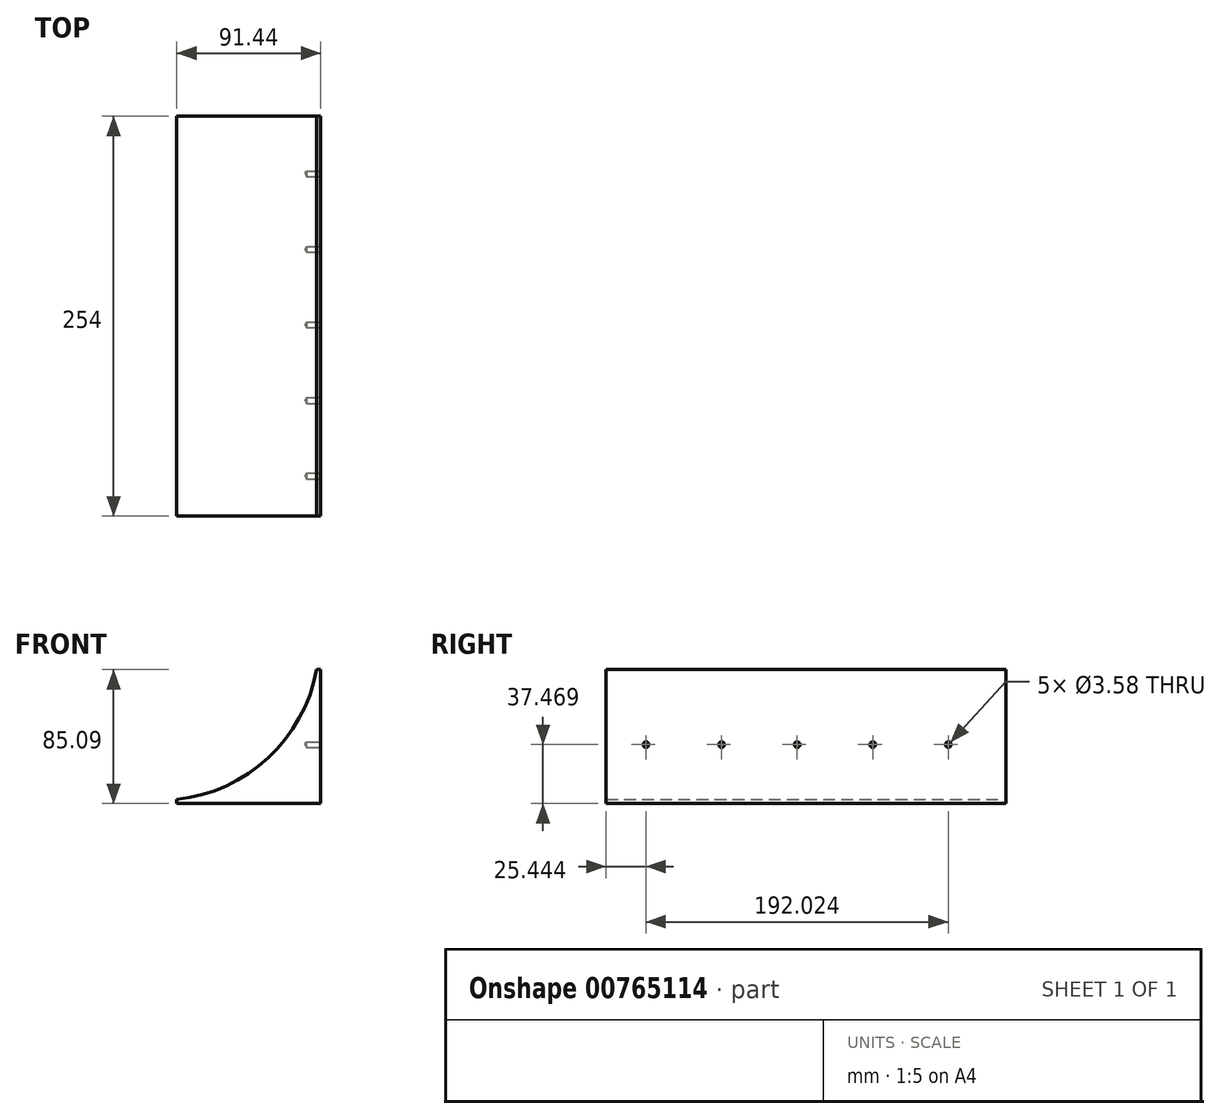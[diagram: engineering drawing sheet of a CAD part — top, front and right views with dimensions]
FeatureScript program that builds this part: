
annotation { "Feature Type Name" : "Feature", "Feature Type Description" : "" }
export const myFeature = defineFeature(function(context is Context, id is Id, definition is map)
    precondition{}
    {
        {
            var Q0;
            Q0=qCreatedBy(makeId("Front.planeOp"),FACE);
            var sketch = newSketch(context, id + "F0", { "sketchPlane" : qUnion([Q0])});
            skLineSegment(sketch, "E0.top", {"start": v(-39.78, -57.04) * mm, "end": v(48.44, -57.04) * mm});
            skLineSegment(sketch, "E1.bottom", {"start": v(49.12, 25.51) * mm, "end": v(61.82, 25.51) * mm});
            skLineSegment(sketch, "E1.top", {"start": v(49.12, -57.04) * mm, "end": v(61.82, -57.04) * mm});
            skLineSegment(sketch, "E1.left", {"start": v(61.82, 25.51) * mm, "end": v(61.82, -57.04) * mm});
            skLineSegment(sketch, "E1.right", {"start": v(49.12, 25.51) * mm, "end": v(49.12, -57.04) * mm});
            skLineSegment(sketch, "E2.bottom", {"start": v(-39.78, -57.04) * mm, "end": v(52.12, -56.76) * mm});
            skLineSegment(sketch, "E3.bottom", {"start": v(-39.78, -57.04) * mm, "end": v(55.47, -57.04) * mm});
            skArc(sketch, "E4", {"start": v(-39.78, -57.04) * mm, "mid": v(18.35, -30.49) * mm, "end": v(49.12, 25.51) * mm});
            skLineSegment(sketch, "E5.bottom", {"start": v(-39.78, -57.04) * mm, "end": v(61.82, -57.04) * mm});
            skLineSegment(sketch, "E5.top", {"start": v(-39.78, -69.74) * mm, "end": v(61.82, -69.74) * mm});
            skLineSegment(sketch, "E5.left", {"start": v(-39.78, -57.04) * mm, "end": v(-39.78, -69.74) * mm});
            skLineSegment(sketch, "E5.right", {"start": v(61.82, -57.04) * mm, "end": v(61.82, -69.74) * mm});
            skSolve(sketch);
        }
        {
            var Q0;
            Q0=qSketchRegion(id+"F0",true);
            extrude(context, id + "F1", {"entities" : qUnion([Q0]), "depth" : 254 * mm, "offsetDistance" : 25.4 * mm});
        }
        {
            var Q0;
            Q0=makeQuery(id+"F1.opExtrude","SWEPT_FACE",FACE,{"disambiguationData":[OSD([sQuery(id+"F0.wireOp",EDGE,"E1.left"),sQuery(id+"F0.wireOp",EDGE,"E5.right")])]});
            var sketch = newSketch(context, id + "F2", { "sketchPlane" : qUnion([Q0])});
            skCircle(sketch, "E6", {"center": v(-228.56, -22.11) * mm, "radius": 1.78 * mm});
            skPoint(sketch, "E6.centerSnap0", {"position": v(-254, -22.11) * mm});
            skCircle(sketch, "E7.1.0.0", {"center": v(-180.55, -22.11) * mm, "radius": 1.78 * mm});
            skCircle(sketch, "E7.2.0.0", {"center": v(-132.54, -22.11) * mm, "radius": 1.78 * mm});
            skCircle(sketch, "E7.3.0.0", {"center": v(-84.54, -22.11) * mm, "radius": 1.78 * mm});
            skCircle(sketch, "E7.4.0.0", {"center": v(-36.53, -22.11) * mm, "radius": 1.78 * mm});
            skLineSegment(sketch, "E7.direction1", {"start": v(-228.56, -22.11) * mm, "end": v(-180.55, -22.11) * mm, "construction": true});
            skSolve(sketch);
        }
        {
            var Q0;
            Q0=sQuery(id+"F2.wireOp",VERTEX,"E6.center");
            var Q1;
            Q1=sQuery(id+"F2.wireOp",VERTEX,"E7.1.0.0.center");
            var Q2;
            Q2=sQuery(id+"F2.wireOp",VERTEX,"E7.2.0.0.center");
            var Q3;
            Q3=sQuery(id+"F2.wireOp",VERTEX,"E7.3.0.0.center");
            var Q4;
            Q4=sQuery(id+"F2.wireOp",VERTEX,"E7.4.0.0.center");
            var Q5;
            Q5=makeQuery(id+"F1.opExtrude","SWEPT_BODY",BODY,{"disambiguationData":[OSD([sQuery(id+"F0.wireOp",EDGE,"E1.bottom"),sQuery(id+"F0.wireOp",EDGE,"E1.left"),sQuery(id+"F0.wireOp",EDGE,"E4"),sQuery(id+"F0.wireOp",EDGE,"E5.top"),sQuery(id+"F0.wireOp",EDGE,"E5.left"),sQuery(id+"F0.wireOp",EDGE,"E5.right")])]});
            hole(context, id + "F3", {"style" : HoleStyle.SIMPLE, "endStyle" : HoleEndStyle.BLIND, "holeDiameter" : 3.58 * mm, "holeDepth" : 19.05 * mm, "isTappedThrough" : true, "tappedDepth" : 12.7 * mm, "tapClearance" : 3, "locations" : qUnion([Q0, Q1, Q2, Q3, Q4]), "scope" : qUnion([Q5])});
        }
        {
            var Q0;
            Q0=makeQuery(id+"F1.opExtrude","SWEPT_FACE",FACE,{"disambiguationData":[OSD([sQuery(id+"F0.wireOp",EDGE,"E1.left"),sQuery(id+"F0.wireOp",EDGE,"E5.right")])]});
            var Q1;
            Q1=makeQuery(id+"F1.opExtrude","CAP_VERTEX",VERTEX,{"disambiguationData":[OSD([sQuery(id+"F0.wireOp",EDGE,"E1.bottom"),sQuery(id+"F0.wireOp",EDGE,"E1.right"),sQuery(id+"F0.wireOp",EDGE,"E4")])],"isStart":false});
            extrude(context, id + "F4", {"entities" : qUnion([Q0]), "operationType" : NewBodyOperationType.REMOVE, "oppositeDirection" : true, "depth" : 10.16 * mm, "endBoundEntityVertex" : qUnion([Q1]), "offsetDistance" : 25.4 * mm});
        }
        {
            var Q0;
            Q0=makeQuery(id+"F1.opExtrude","SWEPT_FACE",FACE,{"disambiguationData":[OSD([sQuery(id+"F0.wireOp",EDGE,"E5.top")])]});
            extrude(context, id + "F5", {"entities" : qUnion([Q0]), "operationType" : NewBodyOperationType.REMOVE, "oppositeDirection" : true, "depth" : 10.16 * mm, "offsetDistance" : 25.4 * mm});
        }
    });
